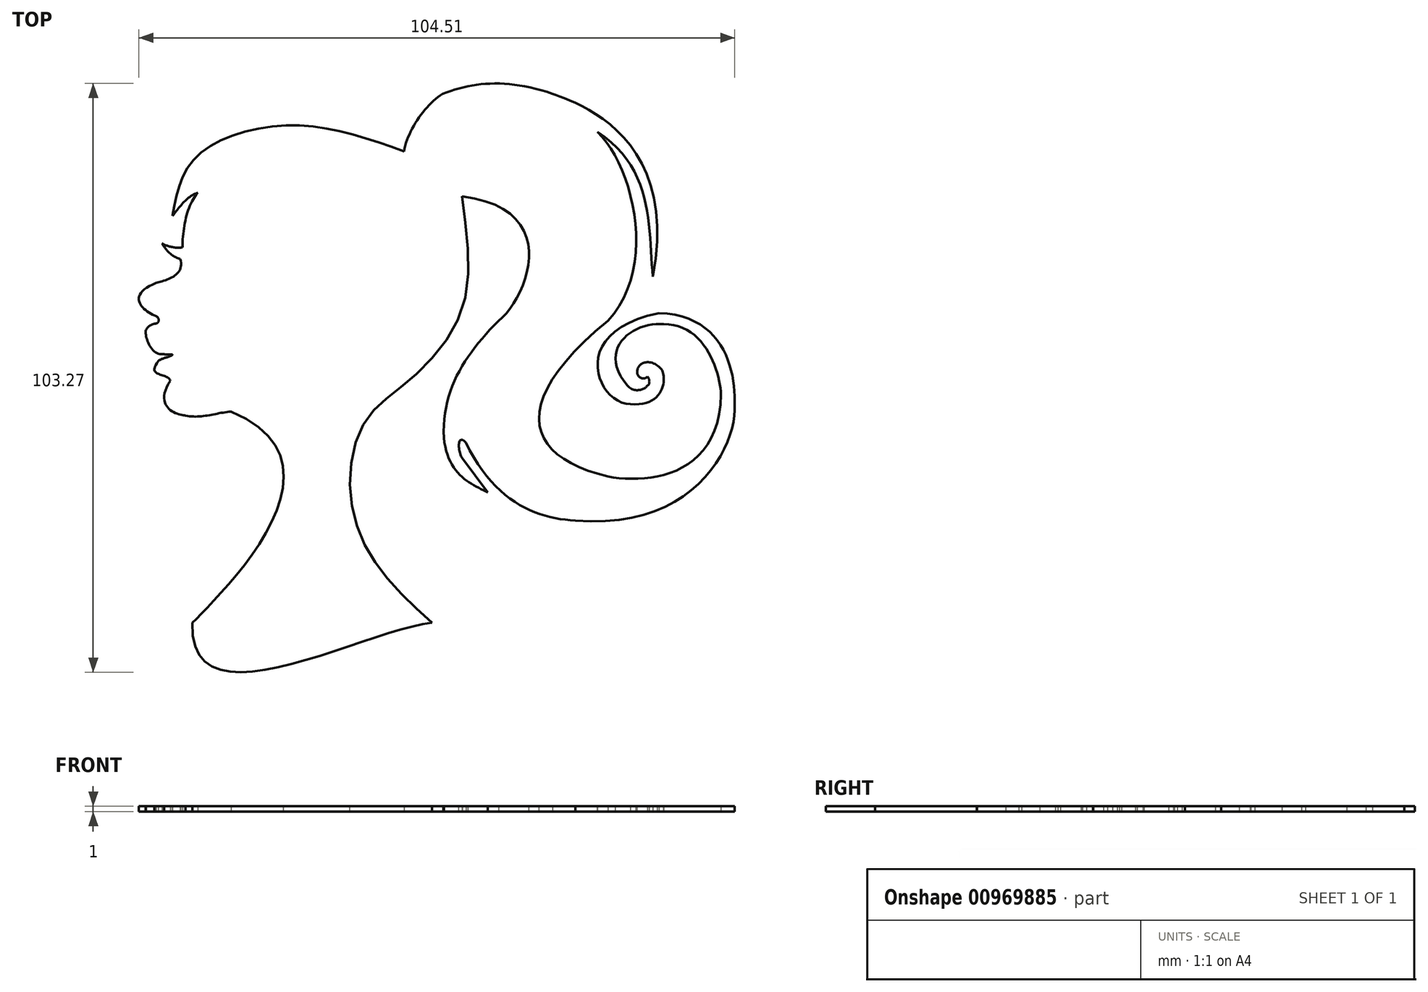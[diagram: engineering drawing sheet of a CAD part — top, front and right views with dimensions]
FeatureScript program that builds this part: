
annotation { "Feature Type Name" : "Feature", "Feature Type Description" : "" }
export const myFeature = defineFeature(function(context is Context, id is Id, definition is map)
    precondition{}
    {
        {
            var Q0;
            Q0=qCreatedBy(makeId("Top.planeOp"),FACE);
            var sketch = newSketch(context, id + "F0", { "sketchPlane" : qUnion([Q0])});
            skFitSpline(sketch, "E0", {"points": [v(-20.87, 18.4) * mm, v(-16.7, 28.7) * mm, v(0, 34.3) * mm, v(19.75, 29.72) * mm], "startDerivative": vector(7.32, 40.63) * mm, "endDerivative": vector(50.74, -18.44) * mm});
            skFitSpline(sketch, "E1", {"points": [v(19.75, 29.72) * mm, v(26.5, 39.83) * mm], "startDerivative": vector(1.98, 11.33) * mm, "endDerivative": vector(9.28, 6.1) * mm});
            skFitSpline(sketch, "E2", {"points": [v(26.5, 39.83) * mm, v(45.83, 39.83) * mm], "startDerivative": vector(16.47, 6.3) * mm, "endDerivative": vector(23.66, -8.13) * mm});
            skFitSpline(sketch, "E3", {"points": [v(45.83, 39.83) * mm, v(63.43, 7.73) * mm], "startDerivative": vector(10.27, -3.87) * mm, "endDerivative": vector(-14.42, -75.8) * mm});
            skFitSpline(sketch, "E4", {"points": [v(63.43, 7.73) * mm, v(53.7, 33.12) * mm], "startDerivative": vector(-2.59, 24.77) * mm, "endDerivative": vector(-30.32, 19.6) * mm});
            skFitSpline(sketch, "E5", {"points": [v(53.7, 33.12) * mm, v(55.5, 0) * mm], "startDerivative": vector(18.78, -17.76) * mm, "endDerivative": vector(-26.4, -28.25) * mm});
            skFitSpline(sketch, "E6", {"points": [v(55.5, 0) * mm, v(55.5, -27.32) * mm], "startDerivative": vector(-52.98, -43.7) * mm, "endDerivative": vector(43.31, -10.55) * mm});
            skFitSpline(sketch, "E7", {"points": [v(55.5, -27.32) * mm, v(75.36, -12.95) * mm], "startDerivative": vector(21.76, -3.96) * mm, "endDerivative": vector(0.88, 43.09) * mm});
            skFitSpline(sketch, "E8", {"points": [v(75.36, -12.95) * mm, v(65.31, -0.6) * mm], "startDerivative": vector(-0.4, 11.94) * mm, "endDerivative": vector(-21.63, -0.37) * mm});
            skFitSpline(sketch, "E9", {"points": [v(65.31, -0.6) * mm, v(58.97, -11.38) * mm], "startDerivative": vector(-14.97, 1.78) * mm, "endDerivative": vector(17, -19.96) * mm});
            skFitSpline(sketch, "E10", {"points": [v(58.97, -11.38) * mm, v(62.48, -11.38) * mm], "startDerivative": vector(3.53, -4.2) * mm, "endDerivative": vector(1.5, 2) * mm});
            skFitSpline(sketch, "E11", {"points": [v(62.48, -11.38) * mm, v(62.48, -9.79) * mm], "startDerivative": vector(1.4, 0.97) * mm, "endDerivative": vector(-1.19, 1.6) * mm});
            skFitSpline(sketch, "E12", {"points": [v(62.48, -9.79) * mm, v(60.71, -8.52) * mm], "startDerivative": vector(-1.23, -1.92) * mm, "endDerivative": vector(1.1, 4.95) * mm});
            skFitSpline(sketch, "E13", {"points": [v(60.71, -8.52) * mm, v(64.93, -8.52) * mm], "startDerivative": vector(0.93, 4.07) * mm, "endDerivative": vector(5.06, -5.94) * mm});
            skFitSpline(sketch, "E14", {"points": [v(64.93, -8.52) * mm, v(59.44, -14.63) * mm], "startDerivative": vector(2.48, -2.88) * mm, "endDerivative": vector(-19.23, 1.57) * mm});
            skFitSpline(sketch, "E15", {"points": [v(59.44, -14.63) * mm, v(64.46, 1.36) * mm], "startDerivative": vector(-17.38, 0.46) * mm, "endDerivative": vector(48.53, 9.98) * mm});
            skFitSpline(sketch, "E16", {"points": [v(64.46, 1.36) * mm, v(77.75, -14.8) * mm], "startDerivative": vector(34.81, -1.2) * mm, "endDerivative": vector(-0.66, -17.59) * mm});
            skFitSpline(sketch, "E17", {"points": [v(77.75, -14.8) * mm, v(49.82, -35.02) * mm], "startDerivative": vector(1.5, -19.36) * mm, "endDerivative": vector(-64.2, 5.72) * mm});
            skFitSpline(sketch, "E18", {"points": [v(49.82, -35.02) * mm, v(30.62, -21.4) * mm], "startDerivative": vector(-20.22, 0.88) * mm, "endDerivative": vector(-15.39, 31.66) * mm});
            skFitSpline(sketch, "E19", {"points": [v(30.62, -21.4) * mm, v(29.99, -24.12) * mm], "startDerivative": vector(-4.57, 5.48) * mm, "endDerivative": vector(2.68, -3.88) * mm});
            skFitSpline(sketch, "E20", {"points": [v(29.99, -24.12) * mm, v(34.46, -30.07) * mm], "startDerivative": vector(4.47, -5.94) * mm, "endDerivative": vector(4.47, -5.94) * mm});
            skFitSpline(sketch, "E21", {"points": [v(34.46, -30.07) * mm, v(26.75, -20.53) * mm], "startDerivative": vector(-8.89, 4.05) * mm, "endDerivative": vector(-1.96, 19.35) * mm});
            skFitSpline(sketch, "E22", {"points": [v(26.75, -20.53) * mm, v(36.34, 0) * mm], "startDerivative": vector(-0.97, 26.16) * mm, "endDerivative": vector(17.46, 17.9) * mm});
            skFitSpline(sketch, "E23", {"points": [v(36.34, 0) * mm, v(29.9, 21.81) * mm], "startDerivative": vector(15.22, 12.11) * mm, "endDerivative": vector(-53.33, 6.27) * mm});
            skFitSpline(sketch, "E24", {"points": [v(29.9, 21.81) * mm, v(29.9, 1.94) * mm, v(20.33, -10.7) * mm, v(12.87, -17.75) * mm, v(10.38, -30.81) * mm, v(15.15, -43.04) * mm, v(24.68, -52.99) * mm], "startDerivative": vector(15.02, -106.62) * mm, "endDerivative": vector(63.2, -57.43) * mm});
            skFitSpline(sketch, "E25", {"points": [v(24.68, -52.99) * mm, v(-17.34, -52.99) * mm], "startDerivative": vector(-35.94, -3.63) * mm, "endDerivative": vector(2.68, 56.5) * mm});
            skFitSpline(sketch, "E26", {"points": [v(-17.34, -52.99) * mm, v(-10.6, -15.92) * mm], "startDerivative": vector(12.76, 13.6) * mm, "endDerivative": vector(-67.4, 28) * mm});
            skFitSpline(sketch, "E27", {"points": [v(-10.6, -15.92) * mm, v(-18.55, -16.61) * mm], "startDerivative": vector(-7.95, -0.7) * mm, "endDerivative": vector(-7.84, 1.83) * mm});
            skFitSpline(sketch, "E28", {"points": [v(-18.55, -16.61) * mm, v(-21.25, -10.51) * mm], "startDerivative": vector(-4.36, 0.14) * mm, "endDerivative": vector(9.2, 14.28) * mm});
            skFitSpline(sketch, "E29", {"points": [v(-21.25, -10.51) * mm, v(-23.33, -7.05) * mm], "startDerivative": vector(-1.43, 4.39) * mm, "endDerivative": vector(6.75, 8.69) * mm});
            skFitSpline(sketch, "E30", {"points": [v(-23.33, -7.05) * mm, v(-20.91, -6.02) * mm], "startDerivative": vector(1.42, 1.32) * mm, "endDerivative": vector(1.63, 0.96) * mm});
            skFitSpline(sketch, "E31", {"points": [v(-20.91, -6.02) * mm, v(-22.42, -5.83) * mm], "startDerivative": vector(0.92, 0.94) * mm, "endDerivative": vector(-2.52, 0.6) * mm});
            skFitSpline(sketch, "E32", {"points": [v(-22.42, -5.83) * mm, v(-25.44, -1.53) * mm], "startDerivative": vector(-7.64, -1.14) * mm, "endDerivative": vector(1.4, 1.17) * mm});
            skFitSpline(sketch, "E33", {"points": [v(-25.44, -1.53) * mm, v(-23.73, -0.47) * mm], "startDerivative": vector(0.93, 1.87) * mm, "endDerivative": vector(2.1, 0.16) * mm});
            skFitSpline(sketch, "E34", {"points": [v(-23.73, -0.47) * mm, v(-23.73, 0.83) * mm], "startDerivative": vector(1.03, -0.05) * mm, "endDerivative": vector(-2.62, 1.63) * mm});
            skFitSpline(sketch, "E35", {"points": [v(-23.73, 0.83) * mm, v(-23.73, 6.66) * mm], "startDerivative": vector(-7.43, 2.72) * mm, "endDerivative": vector(15.93, 6.47) * mm});
            skFitSpline(sketch, "E36", {"points": [v(-23.73, 6.66) * mm, v(-19.52, 10.88) * mm], "startDerivative": vector(5.46, 1.38) * mm, "endDerivative": vector(-2.94, 8.86) * mm});
            skFitSpline(sketch, "E37", {"points": [v(-19.52, 10.88) * mm, v(-22.68, 13.57) * mm], "startDerivative": vector(-4.87, 1.14) * mm, "endDerivative": vector(-1.87, 3.08) * mm});
            skFitSpline(sketch, "E38", {"points": [v(-22.68, 13.57) * mm, v(-19.1, 12.88) * mm], "startDerivative": vector(2.94, -1.74) * mm, "endDerivative": vector(3.38, 0.53) * mm});
            skFitSpline(sketch, "E39", {"points": [v(-19.1, 12.88) * mm, v(-16.4, 22.47) * mm], "startDerivative": vector(0, 10.73) * mm, "endDerivative": vector(5.43, 5.72) * mm});
            skFitSpline(sketch, "E40", {"points": [v(-20.87, 18.4) * mm, v(-16.4, 22.47) * mm], "startDerivative": vector(3.86, 4.7) * mm, "endDerivative": vector(6.16, 2.02) * mm});
            skSolve(sketch);
        }
        {
            var Q0;
            Q0=makeQuery(id+"F0.imprint","IMPRINT",FACE,{"disambiguationData":[TD([[makeQuery(id+"F0.imprint","IMPRINT",EDGE,{"derivedFrom":sQuery(id+"F0.wireOp",EDGE,"E0")}),-1.0]])]});
            extrude(context, id + "F1", {"entities" : qUnion([Q0]), "depth" : 1 * mm, "offsetDistance" : 25 * mm});
        }
    });
